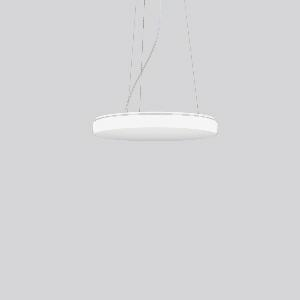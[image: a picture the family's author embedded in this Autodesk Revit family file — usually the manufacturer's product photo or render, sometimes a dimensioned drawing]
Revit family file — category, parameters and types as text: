
# Revit family: flat_polymero_kreis_slim_312091_002_1_1681
name_source: partatom
category: Lighting Fixtures
units: mm (PartAtom-declared; Revit-internal decimal feet)

## family parameters
Cut with Voids When Loaded = No
Host = Face
Light Source = No
Part Type = Normal
Room Calculation Point = No
Round Connector Dimension = Use Diameter
Shared = No

## types (1)
- FLAT POLYMERO KREIS SLIM (1 x LED Modul 830, 3100 lm, 3000)
    Apparent Load = 29 VA
    CIE Flux Codes = 42 72 91 83 100
    Color Rendering = 80
    Color Temperature = 3000
    Default Elevation = 1800 mm
    Description = Series: FLAT POLYMERO KREIS SLIM
Decorative round LED pendant luminaire. Base and canopy: metal, powder-coated, white. Canopy Ø 205 mm, h 35 mm. Diffuser made of non-yellowing plastic (PMMA), opal. Diffuser fastening: patented push system. Homogeneous and smooth light distribution. Suitable for pendant. 3-point steel cable suspension, steplessly adjustable. Special lengths available on request. 
Colour: white
Diameter: 515 mm
Height: 69 mm
Suspension length: 350-1300 mm
Lamp: LED
Socket: without socket
Colour temperature: 3000K
Colour rendering index (CRI): 83
System power: 29 W
Rated luminous flux: 3100 lm
Luminous efficiency: 107 lm/W
Control gear: AC Strom, dim.Ph.an-/abschnitt
Protection class: I
Type of protection: IP 40
    Height = 69 mm
    Lamp = 1 x LED Modul 830
    Lamp Light Flux = 3100 lm
    Lamp count = 1
    Length = 515 mm
    Lifetime = 50000 h
    Luminous efficacy = 107 lm/W
    Manufacturer = RZB
    ModVariant = No
    Model = 312091.002.1
    Mounting Place = Ceiling
    Mounting Type = Pendant
    Number of Poles = 1
    OnlyDefault = Yes
    Power Factor = 1
    Product Name = FLAT POLYMERO KREIS SLIM
    Product group = Pendant luminaires
    ProductGroupID = 902
    Protection Class = Protection class I
    Protection Degree = IP 40
    RLX_Detail_Level = 1
    RLX_Emergency_Light_Flux = 0 lm
    RLX_Emergency_Type = 0
    RLX_Emergency_Type_DB = No
    RlxData = <blob elided: 42253 chars, md5=e224b5c3>
    Socket = socket
    Standby Power = 0 W
    System Light Flux = 3100 lm
    System Power = 29 W
    Type Comments = Product without accessories
    Type Image = 312091.002.jpg
    URL = http://relux.com
    VarID = ---
    Voltage = 230 V
    Voltage Range = 220-240 V
    Weight = 0.00 kg
    Width = 0 mm  [stored 0 ft]

note: [stored X ft] marks values corroborated as IEEE doubles in the binary element streams (Revit-internal decimal feet)

## geometry (parser evidence)
native form markers: Blend x4, Sweep x14
no freeform markers — native parametric forms only
